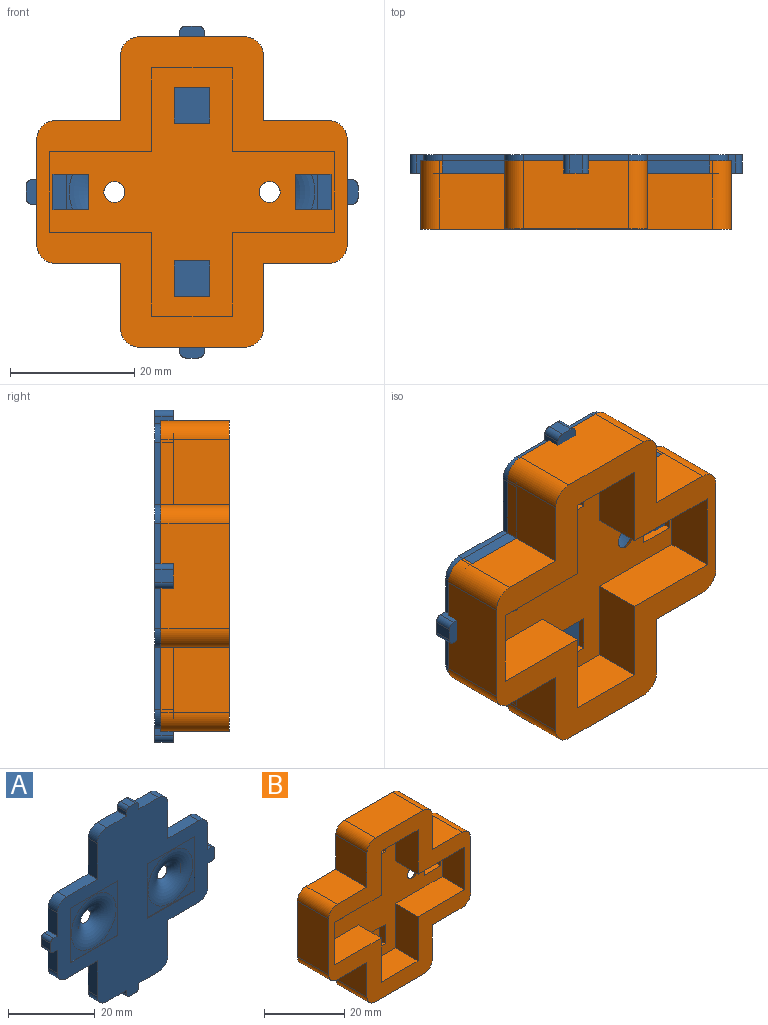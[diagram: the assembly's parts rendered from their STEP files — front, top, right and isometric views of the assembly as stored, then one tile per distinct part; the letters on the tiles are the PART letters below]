
ASSEMBLY  parts=2 mates=1
PART A: 78 faces, bbox 53.5x7.2x53.5 mm
  f0: plane 53.5x53.5mm, normal (0,-1,0), area 1273.3mm2, adj f2,f3,f4,f5,f6,f7,f8,f9
  f1: plane 53.5x53.5mm, normal (0,1,0), area 1594.9mm2, adj f2,f3,f4,f5,f6,f7,f8,f9
  f2: plane 6.5x3mm, normal (0,0,-1), area 19.5mm2, adj f0,f1,f3,f33
  f3: plane 3x1.2mm, normal (-1,0,0), area 3.6mm2, adj f0,f1,f2,f74
  f4: plane 3x2mm, normal (0,0,-1), area 6mm2, adj f0,f1,f74,f75
  f5: plane 3x1.2mm, normal (1,0,0), area 3.6mm2, adj f0,f1,f6,f75
  f6: plane 6.5x3mm, normal (0,0,-1), area 19.5mm2, adj f0,f1,f5,f34
  f7: plane 10.05x3mm, normal (1,0,0), area 30.1mm2, adj f0,f1,f8,f34
  f8: plane 10.05x3mm, normal (0,0,-1), area 30.1mm2, adj f0,f1,f7,f35
  f9: plane 6.5x3mm, normal (1,0,0), area 19.5mm2, adj f0,f1,f10,f35
  f10: plane 3x1.2mm, normal (0,0,-1), area 3.6mm2, adj f0,f1,f9,f72
  f11: plane 3x2mm, normal (1,0,0), area 6mm2, adj f0,f1,f72,f73
  f12: plane 3x1.2mm, normal (0,0,1), area 3.6mm2, adj f0,f1,f13,f73
  f13: plane 6.5x3mm, normal (1,0,0), area 19.5mm2, adj f0,f1,f12,f36
  f14: plane 10.05x3mm, normal (0,0,1), area 30.1mm2, adj f0,f1,f15,f36
  f15: plane 10.05x3mm, normal (1,0,0), area 30.1mm2, adj f0,f1,f14,f37
  f16: plane 6.5x3mm, normal (0,0,1), area 19.5mm2, adj f0,f1,f17,f37
  f17: plane 3x1.2mm, normal (1,0,0), area 3.6mm2, adj f0,f1,f16,f70
  f18: plane 3x2mm, normal (0,0,1), area 6mm2, adj f0,f1,f70,f71
  f19: plane 3x1.2mm, normal (-1,0,0), area 3.6mm2, adj f0,f1,f20,f71
  f20: plane 6.5x3mm, normal (0,0,1), area 19.5mm2, adj f0,f1,f19,f30
  f21: plane 10.05x3mm, normal (-1,0,0), area 30.1mm2, adj f0,f1,f22,f30
  f22: plane 10.05x3mm, normal (0,0,1), area 30.1mm2, adj f0,f1,f21,f31
  f23: plane 6.5x3mm, normal (-1,0,0), area 19.5mm2, adj f0,f1,f24,f31
  f24: plane 3x1.2mm, normal (0,0,1), area 3.6mm2, adj f0,f1,f23,f76
  f25: plane 3x2mm, normal (-1,0,0), area 6mm2, adj f0,f1,f76,f77
  f26: plane 3x1.2mm, normal (0,0,-1), area 3.6mm2, adj f0,f1,f27,f77
  f27: plane 6.5x3mm, normal (-1,0,0), area 19.5mm2, adj f0,f1,f26,f32
  f28: plane 10.05x3mm, normal (0,0,-1), area 30.1mm2, adj f0,f1,f29,f32
  f29: plane 10.05x3mm, normal (-1,0,0), area 30.1mm2, adj f0,f1,f28,f33
  f30: cylinder r=3mm len=3mm, axis (0,1,0), area 14.1mm2, adj f0,f1,f20,f21
  f31: cylinder r=3mm len=3mm, axis (0,1,0), area 14.1mm2, adj f0,f1,f22,f23
  f32: cylinder r=3mm len=3mm, axis (0,1,0), area 14.1mm2, adj f0,f1,f27,f28
  f33: cylinder r=3mm len=3mm, axis (0,1,0), area 14.1mm2, adj f0,f1,f2,f29
  f34: cylinder r=3mm len=3mm, axis (0,1,0), area 14.1mm2, adj f0,f1,f6,f7
  f35: cylinder r=3mm len=3mm, axis (0,1,0), area 14.1mm2, adj f0,f1,f8,f9
  f36: cylinder r=3mm len=3mm, axis (0,1,0), area 14.1mm2, adj f0,f1,f13,f14
  f37: cylinder r=3mm len=3mm, axis (0,1,0), area 14.1mm2, adj f0,f1,f15,f16
  f38: plane 5.8x2mm, normal (0,0,1), area 11.6mm2, adj f1,f39,f41,f42
  f39: plane 5.8x2mm, normal (1,0,0), area 11.6mm2, adj f1,f38,f40,f42
  f40: plane 5.8x2mm, normal (0,0,-1), area 11.6mm2, adj f1,f39,f41,f42
  f41: plane 5.8x2mm, normal (-1,0,0), area 11.6mm2, adj f1,f38,f40,f42
  f42: plane 5.8x5.8mm, normal (0,1,0), area 33.6mm2, adj f38,f39,f40,f41
  f43: plane 5.8x2mm, normal (1,0,0), area 11.6mm2, adj f1,f44,f46,f47
  f44: plane 5.8x2mm, normal (0,0,-1), area 11.6mm2, adj f1,f43,f45,f47
  f45: plane 5.8x2mm, normal (-1,0,0), area 11.6mm2, adj f1,f44,f46,f47
  f46: plane 5.8x2mm, normal (0,0,1), area 11.6mm2, adj f1,f43,f45,f47
  f47: plane 5.8x5.8mm, normal (0,1,0), area 33.6mm2, adj f43,f44,f45,f46
  f48: plane 5.8x2mm, normal (0,0,-1), area 11.6mm2, adj f1,f49,f51,f52
  f49: plane 5.8x2mm, normal (-1,0,0), area 11.6mm2, adj f1,f48,f50,f52
  f50: plane 5.8x2mm, normal (0,0,1), area 11.6mm2, adj f1,f49,f51,f52
  f51: plane 5.8x2mm, normal (1,0,0), area 11.6mm2, adj f1,f48,f50,f52
  f52: plane 5.8x5.8mm, normal (0,1,0), area 33.6mm2, adj f48,f49,f50,f51
  f53: plane 5.8x2mm, normal (0,0,-1), area 11.6mm2, adj f1,f54,f56,f57
  f54: plane 5.8x2mm, normal (-1,0,0), area 11.6mm2, adj f1,f53,f55,f57
  f55: plane 5.8x2mm, normal (0,0,1), area 11.6mm2, adj f1,f54,f56,f57
  f56: plane 5.8x2mm, normal (1,0,0), area 11.6mm2, adj f1,f53,f55,f57
  f57: plane 5.8x5.8mm, normal (0,1,0), area 33.6mm2, adj f53,f54,f55,f56
  f58: plane 15.4x0.2mm, normal (0,0,-1), area 3.1mm2, adj f0,f59,f61,f62
  f59: plane 15.4x0.2mm, normal (1,0,0), area 3.1mm2, adj f0,f58,f60,f62
  f60: plane 15.4x0.2mm, normal (0,0,1), area 3.1mm2, adj f0,f59,f61,f62
  f61: plane 15.4x0.2mm, normal (-1,0,0), area 3.1mm2, adj f0,f58,f60,f62
  f62: plane 15.4x15.4mm, normal (0,-1,0), area 69.7mm2, adj f58,f59,f60,f61,f68
  f63: plane 15.4x0.2mm, normal (0,0,-1), area 3.1mm2, adj f0,f64,f66,f67
  f64: plane 15.4x0.2mm, normal (1,0,0), area 3.1mm2, adj f0,f63,f65,f67
  f65: plane 15.4x0.2mm, normal (0,0,1), area 3.1mm2, adj f0,f64,f66,f67
  f66: plane 15.4x0.2mm, normal (-1,0,0), area 3.1mm2, adj f0,f63,f65,f67
  f67: plane 15.4x15.4mm, normal (0,-1,0), area 69.7mm2, adj f63,f64,f65,f66,f69
  f68: torus R=7.3mm, axis (0,-1,0), area 174.6mm2, adj f1,f62
  f69: torus R=7.3mm, axis (0,-1,0), area 174.6mm2, adj f1,f67
  f70: cylinder r=1mm len=3mm, axis (0,1,0), area 4.7mm2, adj f0,f1,f17,f18
  f71: cylinder r=1mm len=3mm, axis (0,-1,0), area 4.7mm2, adj f0,f1,f18,f19
  f72: cylinder r=1mm len=3mm, axis (0,1,0), area 4.7mm2, adj f0,f1,f10,f11
  f73: cylinder r=1mm len=3mm, axis (0,-1,0), area 4.7mm2, adj f0,f1,f11,f12
  f74: cylinder r=1mm len=3mm, axis (0,1,0), area 4.7mm2, adj f0,f1,f3,f4
  f75: cylinder r=1mm len=3mm, axis (0,-1,0), area 4.7mm2, adj f0,f1,f4,f5
  f76: cylinder r=1mm len=3mm, axis (0,-1,0), area 4.7mm2, adj f0,f1,f24,f25
  f77: cylinder r=1mm len=3mm, axis (0,1,0), area 4.7mm2, adj f0,f1,f25,f26
PART B: 67 faces, bbox 50x11x50 mm
  f0: plane 46x40mm, normal (0,-1,0), area 796.3mm2, adj f14,f15,f16,f17,f18,f19,f20,f21
  f1: plane 50x50mm, normal (0,1,0), area 1281.2mm2, adj f2,f3,f4,f5,f6,f7,f8,f9
  f2: plane 11x10.5mm, normal (0,0,1), area 115.5mm2, adj f1,f13,f26,f27
  f3: plane 17x11mm, normal (-1,0,0), area 187mm2, adj f1,f26,f27,f28
  f4: plane 11x10.5mm, normal (0,0,-1), area 115.5mm2, adj f1,f5,f26,f28
  f5: plane 11x10.5mm, normal (-1,0,0), area 115.5mm2, adj f1,f4,f26,f29
  f6: plane 17x11mm, normal (0,0,-1), area 187mm2, adj f1,f26,f29,f30
  f7: plane 11x10.5mm, normal (1,0,0), area 115.5mm2, adj f1,f8,f26,f30
  f8: plane 11x10.5mm, normal (0,0,-1), area 115.5mm2, adj f1,f7,f26,f31
  f9: plane 17x11mm, normal (1,0,0), area 187mm2, adj f1,f26,f31,f32
  f10: plane 11x10.5mm, normal (0,0,1), area 115.5mm2, adj f1,f11,f26,f32
  f11: plane 11x10.5mm, normal (1,0,0), area 115.5mm2, adj f1,f10,f26,f33
  f12: plane 17x11mm, normal (0,0,1), area 187mm2, adj f1,f26,f33,f34
  f13: plane 11x10.5mm, normal (-1,0,0), area 115.5mm2, adj f1,f2,f26,f34
  f14: plane 13.5x8mm, normal (1,0,0), area 108mm2, adj f0,f15,f25,f26
  f15: plane 13x8mm, normal (0,0,-1), area 104mm2, adj f0,f14,f16,f26
  f16: plane 13.5x8mm, normal (-1,0,0), area 108mm2, adj f0,f15,f17,f26
  f17: plane 16.5x8mm, normal (0,0,-1), area 132mm2, adj f0,f16,f18,f26
  f18: plane 13x8mm, normal (-1,0,0), area 104mm2, adj f0,f17,f19,f26
  f19: plane 16.5x8mm, normal (0,0,1), area 132mm2, adj f0,f18,f20,f26
  f20: plane 13.5x8mm, normal (-1,0,0), area 108mm2, adj f0,f19,f21,f26
  f21: plane 13x8mm, normal (0,0,1), area 104mm2, adj f0,f20,f22,f26
  f22: plane 13.5x8mm, normal (1,0,0), area 108mm2, adj f0,f21,f23,f26
  f23: plane 16.5x8mm, normal (0,0,1), area 132mm2, adj f0,f22,f24,f26
  f24: plane 13x8mm, normal (1,0,0), area 104mm2, adj f0,f23,f25,f26
  f25: plane 16.5x8mm, normal (0,0,-1), area 132mm2, adj f0,f14,f24,f26
  f26: plane 50x50mm, normal (0,-1,0), area 806.5mm2, adj f2,f3,f4,f5,f6,f7,f8,f9
  f27: cylinder r=3mm len=11mm, axis (0,1,0), area 51.8mm2, adj f1,f2,f3,f26
  f28: cylinder r=3mm len=11mm, axis (0,1,0), area 51.8mm2, adj f1,f3,f4,f26
  f29: cylinder r=3mm len=11mm, axis (0,1,0), area 51.8mm2, adj f1,f5,f6,f26
  f30: cylinder r=3mm len=11mm, axis (0,1,0), area 51.8mm2, adj f1,f6,f7,f26
  f31: cylinder r=3mm len=11mm, axis (0,1,0), area 51.8mm2, adj f1,f8,f9,f26
  f32: cylinder r=3mm len=11mm, axis (0,1,0), area 51.8mm2, adj f1,f9,f10,f26
  f33: cylinder r=3mm len=11mm, axis (0,1,0), area 51.8mm2, adj f1,f11,f12,f26
  f34: cylinder r=3mm len=11mm, axis (0,1,0), area 51.8mm2, adj f1,f12,f13,f26
  f35: plane 15.4x0.2mm, normal (0,0,-1), area 3.1mm2, adj f1,f36,f38,f39
  f36: plane 15.4x0.2mm, normal (-1,0,0), area 3.1mm2, adj f1,f35,f37,f39
  f37: plane 15.4x0.2mm, normal (0,0,1), area 3.1mm2, adj f1,f36,f38,f39
  f38: plane 15.4x0.2mm, normal (1,0,0), area 3.1mm2, adj f1,f35,f37,f39
  f39: plane 15.4x15.4mm, normal (0,1,0), area 69.7mm2, adj f35,f36,f37,f38,f65
  f40: plane 15.4x0.2mm, normal (0,0,-1), area 3.1mm2, adj f1,f41,f43,f44
  f41: plane 15.4x0.2mm, normal (-1,0,0), area 3.1mm2, adj f1,f40,f42,f44
  f42: plane 15.4x0.2mm, normal (0,0,1), area 3.1mm2, adj f1,f41,f43,f44
  f43: plane 15.4x0.2mm, normal (1,0,0), area 3.1mm2, adj f1,f40,f42,f44
  f44: plane 15.4x15.4mm, normal (0,1,0), area 69.7mm2, adj f40,f41,f42,f43,f66
  f45: plane 5.8x2mm, normal (0,0,1), area 11.6mm2, adj f0,f46,f48,f49
  f46: plane 5.8x2mm, normal (-1,0,0), area 11.6mm2, adj f0,f45,f47,f49
  f47: plane 5.8x2mm, normal (0,0,-1), area 11.6mm2, adj f0,f46,f48,f49
  f48: plane 5.8x2mm, normal (1,0,0), area 11.6mm2, adj f0,f45,f47,f49
  f49: plane 5.8x5.8mm, normal (0,-1,0), area 33.6mm2, adj f45,f46,f47,f48
  f50: plane 5.8x2mm, normal (-1,0,0), area 11.6mm2, adj f0,f51,f53,f54
  f51: plane 5.8x2mm, normal (0,0,-1), area 11.6mm2, adj f0,f50,f52,f54
  f52: plane 5.8x2mm, normal (1,0,0), area 11.6mm2, adj f0,f51,f53,f54
  f53: plane 5.8x2mm, normal (0,0,1), area 11.6mm2, adj f0,f50,f52,f54
  f54: plane 5.8x5.8mm, normal (0,-1,0), area 33.6mm2, adj f50,f51,f52,f53
  f55: plane 5.8x2mm, normal (0,0,-1), area 11.6mm2, adj f0,f56,f58,f59
  f56: plane 5.8x2mm, normal (1,0,0), area 11.6mm2, adj f0,f55,f57,f59
  f57: plane 5.8x2mm, normal (0,0,1), area 11.6mm2, adj f0,f56,f58,f59
  f58: plane 5.8x2mm, normal (-1,0,0), area 11.6mm2, adj f0,f55,f57,f59
  f59: plane 5.8x5.8mm, normal (0,-1,0), area 33.6mm2, adj f55,f56,f57,f58
  f60: plane 5.8x2mm, normal (0,0,1), area 11.6mm2, adj f0,f61,f63,f64
  f61: plane 5.8x2mm, normal (-1,0,0), area 11.6mm2, adj f0,f60,f62,f64
  f62: plane 5.8x2mm, normal (0,0,-1), area 11.6mm2, adj f0,f61,f63,f64
  f63: plane 5.8x2mm, normal (1,0,0), area 11.6mm2, adj f0,f60,f62,f64
  f64: plane 5.8x5.8mm, normal (0,-1,0), area 33.6mm2, adj f60,f61,f62,f63
  f65: torus R=7.3mm, axis (0,1,0), area 174.6mm2, adj f0,f39
  f66: torus R=7.3mm, axis (0,1,0), area 174.6mm2, adj f0,f44
PLACE A t=(18.05,-0.2,-21.43)mm
PLACE B t=(-10.82,-1.2,-6.33)mm
MATE fastened A.f57 <-> B.f64  axis (0,1,0) through (-38.09,-2.2,6.55)mm
